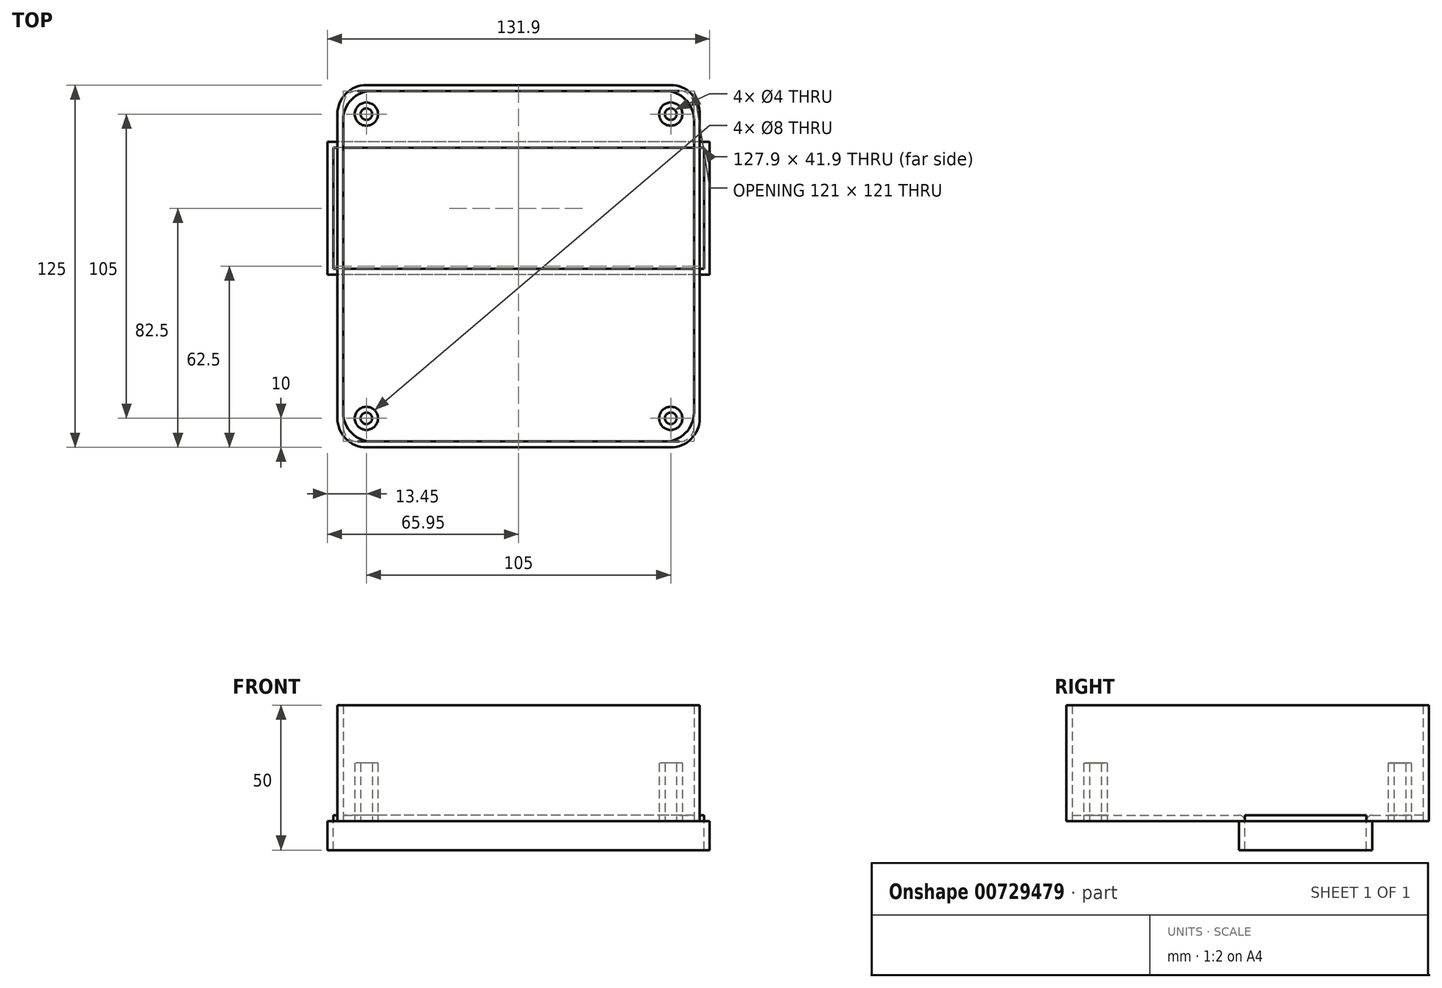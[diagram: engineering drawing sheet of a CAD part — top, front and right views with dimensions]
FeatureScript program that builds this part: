
annotation { "Feature Type Name" : "Feature", "Feature Type Description" : "" }
export const myFeature = defineFeature(function(context is Context, id is Id, definition is map)
    precondition{}
    {
        {
            var Q0;
            Q0=qCreatedBy(makeId("Top.planeOp"),FACE);
            var sketch = newSketch(context, id + "F0", { "sketchPlane" : qUnion([Q0])});
            skLineSegment(sketch, "E0.bottom", {"start": v(60.5, -60.5) * mm, "end": v(-60.5, -60.5) * mm});
            skLineSegment(sketch, "E0.top", {"start": v(60.5, 60.5) * mm, "end": v(-60.5, 60.5) * mm});
            skLineSegment(sketch, "E0.left", {"start": v(60.5, -60.5) * mm, "end": v(60.5, 60.5) * mm});
            skLineSegment(sketch, "E0.right", {"start": v(-60.5, -60.5) * mm, "end": v(-60.5, 60.5) * mm});
            skPoint(sketch, "E0.middle", {"position": v(0, 0) * mm});
            skPoint(sketch, "E1", {"position": v(-52.5, 52.5) * mm});
            skPoint(sketch, "E2", {"position": v(52.5, 52.5) * mm});
            skPoint(sketch, "E3", {"position": v(52.5, -52.5) * mm});
            skPoint(sketch, "E4", {"position": v(-52.5, -52.5) * mm});
            skCircle(sketch, "E5", {"center": v(-52.5, 52.5) * mm, "radius": 4 * mm});
            skCircle(sketch, "E6", {"center": v(52.5, 52.5) * mm, "radius": 4 * mm});
            skCircle(sketch, "E7", {"center": v(52.5, -52.5) * mm, "radius": 4 * mm});
            skCircle(sketch, "E8", {"center": v(-52.5, -52.5) * mm, "radius": 4 * mm});
            skCircle(sketch, "E9", {"center": v(-52.5, 52.5) * mm, "radius": 2 * mm});
            skCircle(sketch, "E10", {"center": v(52.5, 52.5) * mm, "radius": 2 * mm});
            skCircle(sketch, "E11", {"center": v(52.5, -52.5) * mm, "radius": 2 * mm});
            skCircle(sketch, "E12", {"center": v(-52.5, -52.5) * mm, "radius": 2 * mm});
            skLineSegment(sketch, "E13.0", {"start": v(-62.5, -62.5) * mm, "end": v(-62.5, 62.5) * mm});
            skLineSegment(sketch, "E13.1", {"start": v(62.5, -62.5) * mm, "end": v(-62.5, -62.5) * mm});
            skLineSegment(sketch, "E13.2", {"start": v(62.5, -62.5) * mm, "end": v(62.5, 62.5) * mm});
            skLineSegment(sketch, "E13.3", {"start": v(62.5, 62.5) * mm, "end": v(-62.5, 62.5) * mm});
            skPoint(sketch, "E14", {"position": v(0, 20) * mm});
            skLineSegment(sketch, "E15.bottom", {"start": v(65.95, -2.95) * mm, "end": v(-65.95, -2.95) * mm});
            skLineSegment(sketch, "E15.top", {"start": v(65.95, 42.95) * mm, "end": v(-65.95, 42.95) * mm});
            skLineSegment(sketch, "E15.left", {"start": v(65.95, -2.95) * mm, "end": v(65.95, 42.95) * mm});
            skLineSegment(sketch, "E15.right", {"start": v(-65.95, -2.95) * mm, "end": v(-65.95, 42.95) * mm});
            skLineSegment(sketch, "E16.0", {"start": v(63.95, 40.95) * mm, "end": v(-63.95, 40.95) * mm});
            skLineSegment(sketch, "E16.1", {"start": v(63.95, -0.95) * mm, "end": v(63.95, 40.95) * mm});
            skLineSegment(sketch, "E16.2", {"start": v(63.95, -0.95) * mm, "end": v(-63.95, -0.95) * mm});
            skLineSegment(sketch, "E16.3", {"start": v(-63.95, -0.95) * mm, "end": v(-63.95, 40.95) * mm});
            skSolve(sketch);
        }
        {
            var Q0;
            {var subQ0=sQuery(id+"F0.wireOp",EDGE,"E0.top");Q0=makeQuery(id+"F0.imprint","IMPRINT",FACE,{"disambiguationData":[TD([[makeQuery(id+"F0.imprint","IMPRINT",EDGE,{"derivedFrom":subQ0}),1.0]])]});}
            var Q1;
            {var subQ1=sQuery(id+"F0.wireOp",EDGE,"E0.bottom");Q1=makeQuery(id+"F0.imprint","IMPRINT",FACE,{"disambiguationData":[TD([[makeQuery(id+"F0.imprint","IMPRINT",EDGE,{"derivedFrom":subQ1}),-1.0]])]});}
            var Q2;
            {var subQ0=sQuery(id+"F0.wireOp",EDGE,"E15.bottom");var subQ1=sQuery(id+"F0.wireOp",EDGE,"E0.left");var subQ2=makeQuery(id+"F0.imprint","INTERSECT",VERTEX,{"derivedFrom":[subQ1,subQ0]});Q2=makeQuery(id+"F0.imprint","IMPRINT",FACE,{"disambiguationData":[TD([[makeQuery(id+"F0.imprint","IMPRINT",EDGE,{"disambiguationData":[TD([[subQ2,-1.0]])],"derivedFrom":subQ1}),1.0]])]});}
            var Q3;
            {var subQ0=sQuery(id+"F0.wireOp",EDGE,"E16.0");var subQ1=sQuery(id+"F0.wireOp",EDGE,"E0.left");var subQ2=makeQuery(id+"F0.imprint","INTERSECT",VERTEX,{"derivedFrom":[subQ1,subQ0]});Q3=makeQuery(id+"F0.imprint","IMPRINT",FACE,{"disambiguationData":[TD([[makeQuery(id+"F0.imprint","IMPRINT",EDGE,{"disambiguationData":[TD([[subQ2,-1.0]])],"derivedFrom":subQ1}),1.0]])]});}
            var Q4;
            {var subQ5=sQuery(id+"F0.wireOp",EDGE,"E16.3");Q4=makeQuery(id+"F0.imprint","IMPRINT",FACE,{"disambiguationData":[TD([[makeQuery(id+"F0.imprint","IMPRINT",EDGE,{"derivedFrom":subQ5}),-1.0]])]});}
            var Q5;
            {var subQ5=sQuery(id+"F0.wireOp",EDGE,"E16.1");Q5=makeQuery(id+"F0.imprint","IMPRINT",FACE,{"disambiguationData":[TD([[makeQuery(id+"F0.imprint","IMPRINT",EDGE,{"derivedFrom":subQ5}),1.0]])]});}
            extrude(context, id + "F1", {"entities" : qUnion([Q0, Q1, Q2, Q3, Q4, Q5]), "depth" : 2 * mm, "offsetDistance" : 25 * mm});
        }
        {
            var Q0;
            {var subQ5=sQuery(id+"F0.wireOp",EDGE,"E0.top");Q0=makeQuery(id+"F0.imprint","IMPRINT",FACE,{"disambiguationData":[TD([[makeQuery(id+"F0.imprint","IMPRINT",EDGE,{"derivedFrom":subQ5}),-1.0]])]});}
            var Q1;
            {var subQ0=sQuery(id+"F0.wireOp",EDGE,"E16.0");var subQ1=sQuery(id+"F0.wireOp",EDGE,"E0.right");var subQ2=makeQuery(id+"F0.imprint","INTERSECT",VERTEX,{"derivedFrom":[subQ1,subQ0]});Q1=makeQuery(id+"F0.imprint","IMPRINT",FACE,{"disambiguationData":[TD([[makeQuery(id+"F0.imprint","IMPRINT",EDGE,{"disambiguationData":[TD([[subQ2,-1.0]])],"derivedFrom":subQ1}),1.0]])]});}
            var Q2;
            {var subQ0=sQuery(id+"F0.wireOp",EDGE,"E16.2");var subQ1=sQuery(id+"F0.wireOp",EDGE,"E0.right");var subQ2=makeQuery(id+"F0.imprint","INTERSECT",VERTEX,{"derivedFrom":[subQ1,subQ0]});Q2=makeQuery(id+"F0.imprint","IMPRINT",FACE,{"disambiguationData":[TD([[makeQuery(id+"F0.imprint","IMPRINT",EDGE,{"disambiguationData":[TD([[subQ2,-1.0]])],"derivedFrom":subQ1}),1.0]])]});}
            var Q3;
            {var subQ1=sQuery(id+"F0.wireOp",EDGE,"E0.bottom");Q3=makeQuery(id+"F0.imprint","IMPRINT",FACE,{"disambiguationData":[TD([[makeQuery(id+"F0.imprint","IMPRINT",EDGE,{"derivedFrom":subQ1}),1.0]])]});}
            var Q4;
            {var subQ0=sQuery(id+"F0.wireOp",EDGE,"E15.bottom");var subQ1=sQuery(id+"F0.wireOp",EDGE,"E0.right");var subQ2=makeQuery(id+"F0.imprint","INTERSECT",VERTEX,{"derivedFrom":[subQ1,subQ0]});Q4=makeQuery(id+"F0.imprint","IMPRINT",FACE,{"disambiguationData":[TD([[makeQuery(id+"F0.imprint","IMPRINT",EDGE,{"disambiguationData":[TD([[subQ2,-1.0]])],"derivedFrom":subQ1}),1.0]])]});}
            var Q5;
            {var subQ0=sQuery(id+"F0.wireOp",EDGE,"E15.bottom");var subQ1=sQuery(id+"F0.wireOp",EDGE,"E0.left");var subQ2=makeQuery(id+"F0.imprint","INTERSECT",VERTEX,{"derivedFrom":[subQ1,subQ0]});Q5=makeQuery(id+"F0.imprint","IMPRINT",FACE,{"disambiguationData":[TD([[makeQuery(id+"F0.imprint","IMPRINT",EDGE,{"disambiguationData":[TD([[subQ2,-1.0]])],"derivedFrom":subQ1}),-1.0]])]});}
            var Q6;
            {var subQ0=sQuery(id+"F0.wireOp",EDGE,"E16.2");var subQ1=sQuery(id+"F0.wireOp",EDGE,"E0.left");var subQ2=makeQuery(id+"F0.imprint","INTERSECT",VERTEX,{"derivedFrom":[subQ1,subQ0]});Q6=makeQuery(id+"F0.imprint","IMPRINT",FACE,{"disambiguationData":[TD([[makeQuery(id+"F0.imprint","IMPRINT",EDGE,{"disambiguationData":[TD([[subQ2,-1.0]])],"derivedFrom":subQ1}),-1.0]])]});}
            var Q7;
            {var subQ0=sQuery(id+"F0.wireOp",EDGE,"E16.0");var subQ1=sQuery(id+"F0.wireOp",EDGE,"E0.left");var subQ2=makeQuery(id+"F0.imprint","INTERSECT",VERTEX,{"derivedFrom":[subQ1,subQ0]});Q7=makeQuery(id+"F0.imprint","IMPRINT",FACE,{"disambiguationData":[TD([[makeQuery(id+"F0.imprint","IMPRINT",EDGE,{"disambiguationData":[TD([[subQ2,-1.0]])],"derivedFrom":subQ1}),-1.0]])]});}
            extrude(context, id + "F2", {"entities" : qUnion([Q0, Q1, Q2, Q3, Q4, Q5, Q6, Q7]), "depth" : 40 * mm, "offsetDistance" : 25 * mm});
        }
        {
            var Q0;
            Q0=makeQuery(id+"F0.imprint","IMPRINT",FACE,{"disambiguationData":[TD([[makeQuery(id+"F0.imprint","IMPRINT",EDGE,{"derivedFrom":sQuery(id+"F0.wireOp",EDGE,"E5")}),1.0]])]});
            var Q1;
            Q1=makeQuery(id+"F0.imprint","IMPRINT",FACE,{"disambiguationData":[TD([[makeQuery(id+"F0.imprint","IMPRINT",EDGE,{"derivedFrom":sQuery(id+"F0.wireOp",EDGE,"E6")}),1.0]])]});
            var Q2;
            Q2=makeQuery(id+"F0.imprint","IMPRINT",FACE,{"disambiguationData":[TD([[makeQuery(id+"F0.imprint","IMPRINT",EDGE,{"derivedFrom":sQuery(id+"F0.wireOp",EDGE,"E7")}),1.0]])]});
            var Q3;
            Q3=makeQuery(id+"F0.imprint","IMPRINT",FACE,{"disambiguationData":[TD([[makeQuery(id+"F0.imprint","IMPRINT",EDGE,{"derivedFrom":sQuery(id+"F0.wireOp",EDGE,"E8")}),1.0]])]});
            extrude(context, id + "F3", {"entities" : qUnion([Q0, Q1, Q2, Q3]), "depth" : 20 * mm, "offsetDistance" : 25 * mm});
        }
        {
            var Q0;
            {var subQ5=sQuery(id+"F0.wireOp",EDGE,"E15.right");Q0=makeQuery(id+"F0.imprint","IMPRINT",FACE,{"disambiguationData":[TD([[makeQuery(id+"F0.imprint","IMPRINT",EDGE,{"derivedFrom":subQ5}),-1.0]])]});}
            var Q1;
            {var subQ0=sQuery(id+"F0.wireOp",EDGE,"E15.bottom");var subQ1=sQuery(id+"F0.wireOp",EDGE,"E0.right");var subQ2=makeQuery(id+"F0.imprint","INTERSECT",VERTEX,{"derivedFrom":[subQ1,subQ0]});Q1=makeQuery(id+"F0.imprint","IMPRINT",FACE,{"disambiguationData":[TD([[makeQuery(id+"F0.imprint","IMPRINT",EDGE,{"disambiguationData":[TD([[subQ2,-1.0]])],"derivedFrom":subQ1}),1.0]])]});}
            var Q2;
            {var subQ0=sQuery(id+"F0.wireOp",EDGE,"E16.0");var subQ1=sQuery(id+"F0.wireOp",EDGE,"E0.right");var subQ2=makeQuery(id+"F0.imprint","INTERSECT",VERTEX,{"derivedFrom":[subQ1,subQ0]});Q2=makeQuery(id+"F0.imprint","IMPRINT",FACE,{"disambiguationData":[TD([[makeQuery(id+"F0.imprint","IMPRINT",EDGE,{"disambiguationData":[TD([[subQ2,-1.0]])],"derivedFrom":subQ1}),1.0]])]});}
            var Q3;
            {var subQ0=sQuery(id+"F0.wireOp",EDGE,"E15.bottom");var subQ1=sQuery(id+"F0.wireOp",EDGE,"E0.left");var subQ2=makeQuery(id+"F0.imprint","INTERSECT",VERTEX,{"derivedFrom":[subQ1,subQ0]});Q3=makeQuery(id+"F0.imprint","IMPRINT",FACE,{"disambiguationData":[TD([[makeQuery(id+"F0.imprint","IMPRINT",EDGE,{"disambiguationData":[TD([[subQ2,-1.0]])],"derivedFrom":subQ1}),1.0]])]});}
            var Q4;
            {var subQ0=sQuery(id+"F0.wireOp",EDGE,"E16.0");var subQ1=sQuery(id+"F0.wireOp",EDGE,"E0.left");var subQ2=makeQuery(id+"F0.imprint","INTERSECT",VERTEX,{"derivedFrom":[subQ1,subQ0]});Q4=makeQuery(id+"F0.imprint","IMPRINT",FACE,{"disambiguationData":[TD([[makeQuery(id+"F0.imprint","IMPRINT",EDGE,{"disambiguationData":[TD([[subQ2,-1.0]])],"derivedFrom":subQ1}),1.0]])]});}
            var Q5;
            {var subQ0=sQuery(id+"F0.wireOp",EDGE,"E15.bottom");var subQ1=sQuery(id+"F0.wireOp",EDGE,"E0.left");var subQ2=makeQuery(id+"F0.imprint","INTERSECT",VERTEX,{"derivedFrom":[subQ1,subQ0]});Q5=makeQuery(id+"F0.imprint","IMPRINT",FACE,{"disambiguationData":[TD([[makeQuery(id+"F0.imprint","IMPRINT",EDGE,{"disambiguationData":[TD([[subQ2,-1.0]])],"derivedFrom":subQ1}),-1.0]])]});}
            var Q6;
            {var subQ0=sQuery(id+"F0.wireOp",EDGE,"E16.0");var subQ1=sQuery(id+"F0.wireOp",EDGE,"E0.left");var subQ2=makeQuery(id+"F0.imprint","INTERSECT",VERTEX,{"derivedFrom":[subQ1,subQ0]});Q6=makeQuery(id+"F0.imprint","IMPRINT",FACE,{"disambiguationData":[TD([[makeQuery(id+"F0.imprint","IMPRINT",EDGE,{"disambiguationData":[TD([[subQ2,-1.0]])],"derivedFrom":subQ1}),-1.0]])]});}
            var Q7;
            {var subQ5=sQuery(id+"F0.wireOp",EDGE,"E15.left");Q7=makeQuery(id+"F0.imprint","IMPRINT",FACE,{"disambiguationData":[TD([[makeQuery(id+"F0.imprint","IMPRINT",EDGE,{"derivedFrom":subQ5}),1.0]])]});}
            extrude(context, id + "F4", {"entities" : qUnion([Q0, Q1, Q2, Q3, Q4, Q5, Q6, Q7]), "oppositeDirection" : true, "depth" : 10 * mm, "offsetDistance" : 25 * mm});
        }
        {
            var Q0;
            Q0=makeQuery(id+"F2.opExtrude","SWEPT_EDGE",EDGE,{"disambiguationData":[OSD([sQuery(id+"F0.wireOp",EDGE,"E0.top"),sQuery(id+"F0.wireOp",EDGE,"E0.right")])]});
            var Q1;
            Q1=makeQuery(id+"F2.opExtrude","SWEPT_EDGE",EDGE,{"disambiguationData":[OSD([sQuery(id+"F0.wireOp",EDGE,"E0.top"),sQuery(id+"F0.wireOp",EDGE,"E0.left")])]});
            var Q2;
            Q2=makeQuery(id+"F2.opExtrude","SWEPT_EDGE",EDGE,{"disambiguationData":[OSD([sQuery(id+"F0.wireOp",EDGE,"E0.bottom"),sQuery(id+"F0.wireOp",EDGE,"E0.right")])]});
            var Q3;
            Q3=makeQuery(id+"F2.opExtrude","SWEPT_EDGE",EDGE,{"disambiguationData":[OSD([sQuery(id+"F0.wireOp",EDGE,"E0.bottom"),sQuery(id+"F0.wireOp",EDGE,"E0.left")])]});
            var Q4;
            Q4=makeQuery(id+"F2.opExtrude","SWEPT_EDGE",EDGE,{"disambiguationData":[OSD([sQuery(id+"F0.wireOp",EDGE,"E13.0"),sQuery(id+"F0.wireOp",EDGE,"E13.3")])]});
            var Q5;
            Q5=makeQuery(id+"F2.opExtrude","SWEPT_EDGE",EDGE,{"disambiguationData":[OSD([sQuery(id+"F0.wireOp",EDGE,"E13.2"),sQuery(id+"F0.wireOp",EDGE,"E13.3")])]});
            var Q6;
            Q6=makeQuery(id+"F2.opExtrude","SWEPT_EDGE",EDGE,{"disambiguationData":[OSD([sQuery(id+"F0.wireOp",EDGE,"E13.1"),sQuery(id+"F0.wireOp",EDGE,"E13.2")])]});
            var Q7;
            Q7=makeQuery(id+"F2.opExtrude","SWEPT_EDGE",EDGE,{"disambiguationData":[OSD([sQuery(id+"F0.wireOp",EDGE,"E13.0"),sQuery(id+"F0.wireOp",EDGE,"E13.1")])]});
            fillet(context, id + "F5", {"entities" : qUnion([Q0, Q1, Q2, Q3, Q4, Q5, Q6, Q7]), "radius" : 10 * mm, "tangentPropagation" : true, "allowEdgeOverflow" : false});
        }
        {
            var Q0;
            {var subQ0=sQuery(id+"F0.wireOp",EDGE,"E16.2");Q0=makeQuery(id+"F1.opExtrude","CAP_EDGE",EDGE,{"disambiguationData":[OSD([subQ0]),TDD([makeQuery(id+"F0.imprint","IMPRINT",EDGE,{"disambiguationData":[TD([[makeQuery(id+"F0.imprint","INTERSECT",VERTEX,{"derivedFrom":[sQuery(id+"F0.wireOp",EDGE,"E0.left"),subQ0]}),-1.0]])],"derivedFrom":subQ0})])],"isStart":false});}
            var Q1;
            {var subQ0=sQuery(id+"F0.wireOp",EDGE,"E16.0");Q1=makeQuery(id+"F1.opExtrude","CAP_EDGE",EDGE,{"disambiguationData":[OSD([subQ0]),TDD([makeQuery(id+"F0.imprint","IMPRINT",EDGE,{"disambiguationData":[TD([[makeQuery(id+"F0.imprint","INTERSECT",VERTEX,{"derivedFrom":[sQuery(id+"F0.wireOp",EDGE,"E0.left"),subQ0]}),-1.0]])],"derivedFrom":subQ0})])],"isStart":false});}
            fillet(context, id + "F6", {"entities" : qUnion([Q0, Q1]), "radius" : 2 * mm, "tangentPropagation" : true, "allowEdgeOverflow" : false});
        }
        {
            var Q0;
            Q0=makeQuery(id+"F1.opExtrude","SWEPT_EDGE",EDGE,{"disambiguationData":[OSD([sQuery(id+"F0.wireOp",EDGE,"E0.top"),sQuery(id+"F0.wireOp",EDGE,"E0.left")])]});
            var Q1;
            Q1=makeQuery(id+"F1.opExtrude","SWEPT_EDGE",EDGE,{"disambiguationData":[OSD([sQuery(id+"F0.wireOp",EDGE,"E0.top"),sQuery(id+"F0.wireOp",EDGE,"E0.right")])]});
            var Q2;
            Q2=makeQuery(id+"F1.opExtrude","SWEPT_EDGE",EDGE,{"disambiguationData":[OSD([sQuery(id+"F0.wireOp",EDGE,"E0.bottom"),sQuery(id+"F0.wireOp",EDGE,"E0.right")])]});
            var Q3;
            Q3=makeQuery(id+"F1.opExtrude","SWEPT_EDGE",EDGE,{"disambiguationData":[OSD([sQuery(id+"F0.wireOp",EDGE,"E0.bottom"),sQuery(id+"F0.wireOp",EDGE,"E0.left")])]});
            fillet(context, id + "F7", {"entities" : qUnion([Q0, Q1, Q2, Q3]), "radius" : 5 * mm, "tangentPropagation" : true, "allowEdgeOverflow" : false});
        }
    });
